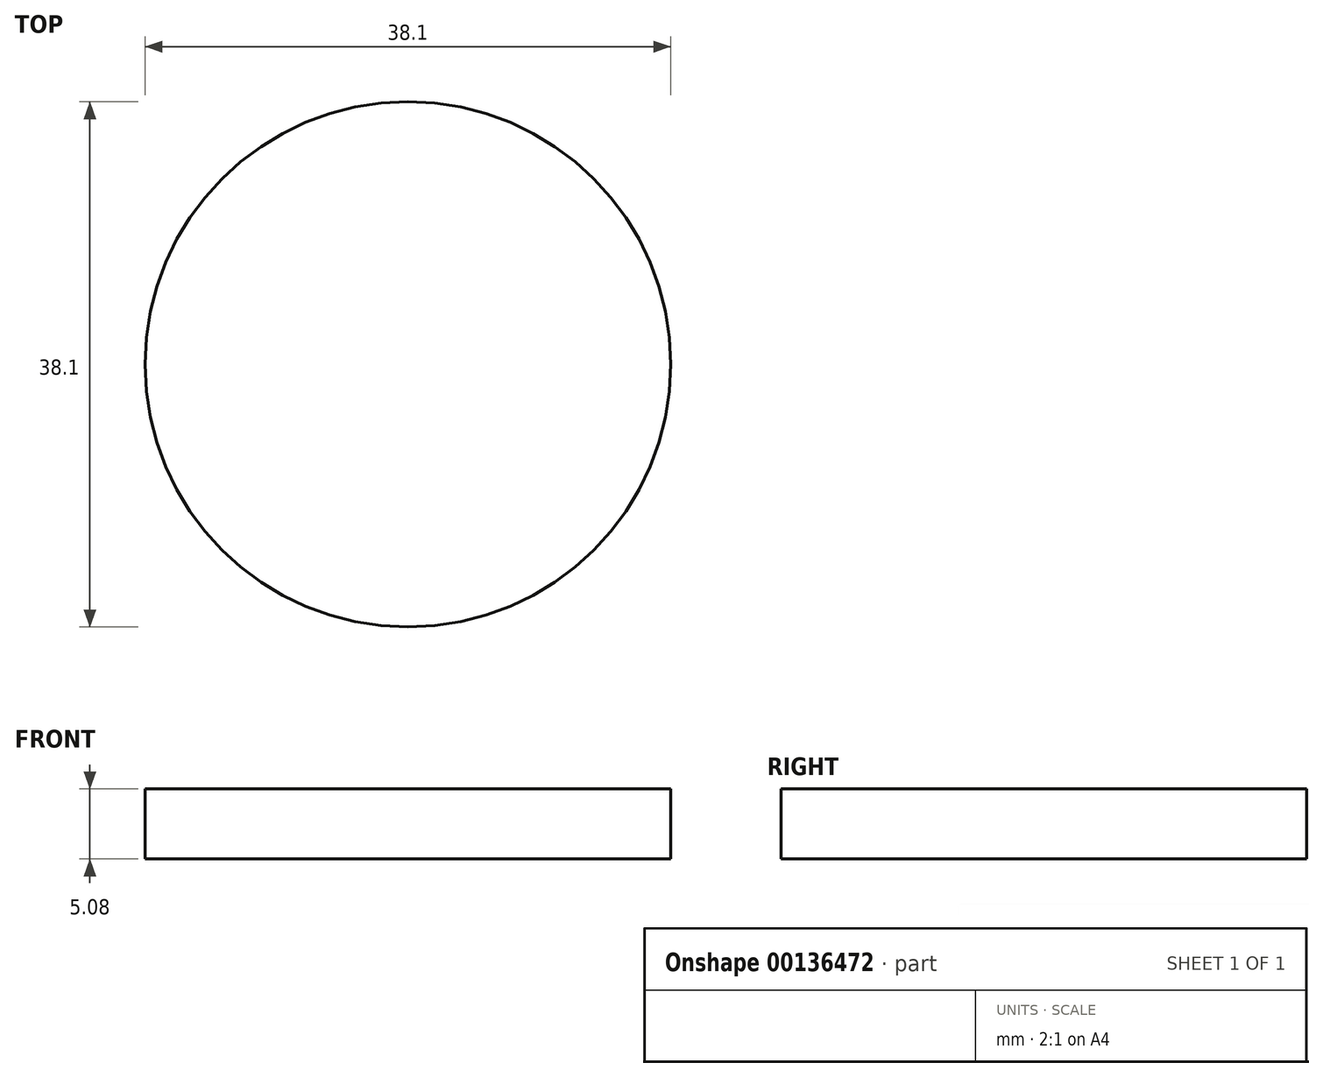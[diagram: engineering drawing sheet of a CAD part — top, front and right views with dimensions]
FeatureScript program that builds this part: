
annotation { "Feature Type Name" : "Feature", "Feature Type Description" : "" }
export const myFeature = defineFeature(function(context is Context, id is Id, definition is map)
    precondition{}
    {
        {
            var Q0;
            Q0=qCreatedBy(makeId("Top.planeOp"),FACE);
            var sketch = newSketch(context, id + "F0", { "sketchPlane" : qUnion([Q0])});
            skCircle(sketch, "E0", {"center": v(0, 0) * mm, "radius": 19.05 * mm});
            skSolve(sketch);
        }
        {
            var Q0;
            Q0=makeQuery(id+"F0.imprint","IMPRINT",FACE,{"disambiguationData":[TD([[makeQuery(id+"F0.imprint","IMPRINT",EDGE,{"derivedFrom":sQuery(id+"F0.wireOp",EDGE,"E0")}),1.0]])]});
            extrude(context, id + "F1", {"entities" : qUnion([Q0]), "depth" : 5.08 * mm});
        }
    });
